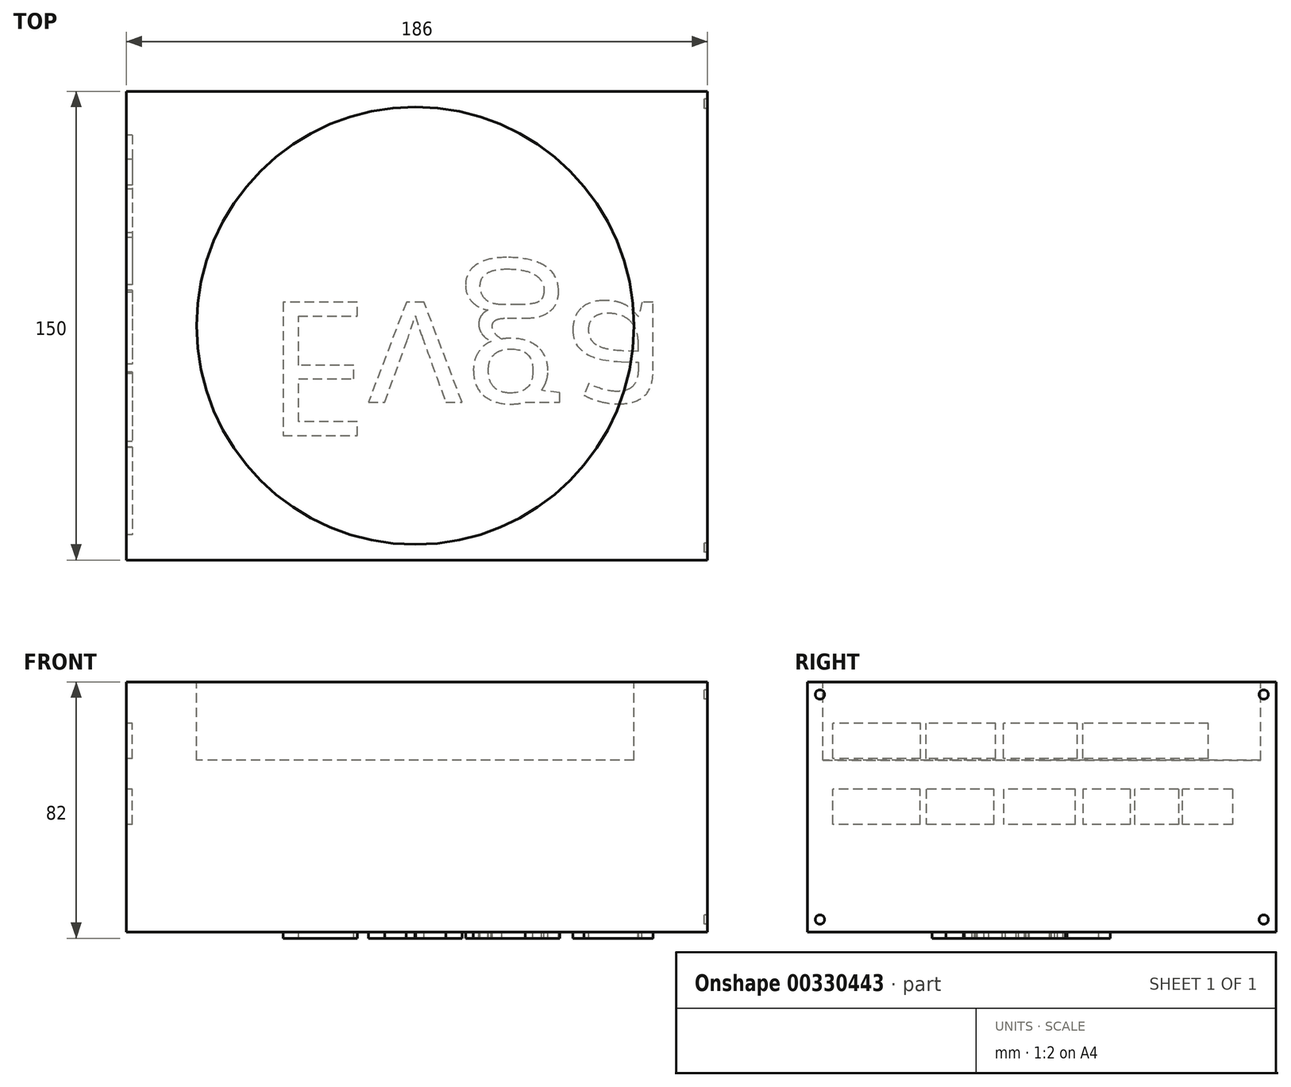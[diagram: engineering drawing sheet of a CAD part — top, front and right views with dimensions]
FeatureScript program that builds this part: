
annotation { "Feature Type Name" : "Feature", "Feature Type Description" : "" }
export const myFeature = defineFeature(function(context is Context, id is Id, definition is map)
    precondition{}
    {
        {
            var Q0;
            Q0=qCreatedBy(makeId("Top.planeOp"),FACE);
            var sketch = newSketch(context, id + "F0", { "sketchPlane" : qUnion([Q0])});
            skLineSegment(sketch, "E0.bottom", {"start": v(-3593.2, 0) * mm, "end": v(-3408.2, 0) * mm});
            skLineSegment(sketch, "E0.top", {"start": v(-3593.2, 150) * mm, "end": v(-3408.2, 150) * mm});
            skLineSegment(sketch, "E0.left", {"start": v(-3593.2, 0) * mm, "end": v(-3593.2, 150) * mm});
            skLineSegment(sketch, "E0.right", {"start": v(-3408.2, 0) * mm, "end": v(-3408.2, 150) * mm});
            skSolve(sketch);
        }
        {
            var Q0;
            Q0=makeQuery(id+"F0.imprint","IMPRINT",FACE,{"disambiguationData":[TD([[makeQuery(id+"F0.imprint","IMPRINT",EDGE,{"derivedFrom":sQuery(id+"F0.wireOp",EDGE,"E0.bottom")}),1.0]])]});
            extrude(context, id + "F1", {"entities" : qUnion([Q0]), "depth" : 80 * mm});
        }
        {
            var Q0;
            Q0=makeQuery(id+"F1.opExtrude","CAP_FACE",FACE,{"disambiguationData":[OSD([sQuery(id+"F0.wireOp",EDGE,"E0.bottom"),sQuery(id+"F0.wireOp",EDGE,"E0.top"),sQuery(id+"F0.wireOp",EDGE,"E0.left"),sQuery(id+"F0.wireOp",EDGE,"E0.right")])],"isStart":false});
            var sketch = newSketch(context, id + "F2", { "sketchPlane" : qUnion([Q0])});
            skLineSegment(sketch, "E1", {"start": v(-3593.2, 150) * mm, "end": v(-3408.2, 0) * mm, "construction": true});
            skCircle(sketch, "E2", {"center": v(-3500.7, 75) * mm, "radius": 70 * mm});
            skSolve(sketch);
        }
        {
            var Q0;
            Q0=makeQuery(id+"F2.imprint","IMPRINT",FACE,{"disambiguationData":[TD([[makeQuery(id+"F2.imprint","IMPRINT",EDGE,{"derivedFrom":sQuery(id+"F2.wireOp",EDGE,"E2")}),1.0]])]});
            extrude(context, id + "F3", {"entities" : qUnion([Q0]), "operationType" : NewBodyOperationType.REMOVE, "oppositeDirection" : true, "depth" : 25 * mm});
        }
        {
            var Q0;
            Q0=makeQuery(id+"F1.opExtrude","SWEPT_FACE",FACE,{"disambiguationData":[OSD([sQuery(id+"F0.wireOp",EDGE,"E0.right")])]});
            var sketch = newSketch(context, id + "F4", { "sketchPlane" : qUnion([Q0])});
            skLineSegment(sketch, "E3", {"start": v(0, 0) * mm, "end": v(0, 6) * mm});
            skLineSegment(sketch, "E4.bottom", {"start": v(114, 7.67) * mm, "end": v(126, 7.67) * mm});
            skLineSegment(sketch, "E4.top", {"start": v(114, 12.33) * mm, "end": v(126, 12.33) * mm});
            skLineSegment(sketch, "E4.right", {"start": v(126, 7.67) * mm, "end": v(126, 12.33) * mm});
            skLineSegment(sketch, "E5.bottom", {"start": v(116.68, 8.25) * mm, "end": v(123.32, 8.25) * mm});
            skLineSegment(sketch, "E5.top", {"start": v(116.68, 11.75) * mm, "end": v(123.32, 11.75) * mm});
            skLineSegment(sketch, "E5.right", {"start": v(123.32, 8.25) * mm, "end": v(123.32, 11.75) * mm});
            skLineSegment(sketch, "E6.bottom", {"start": v(114.02, 42.62) * mm, "end": v(125.98, 42.62) * mm});
            skLineSegment(sketch, "E6.top", {"start": v(114.02, 45.11) * mm, "end": v(125.98, 45.11) * mm});
            skLineSegment(sketch, "E6.right", {"start": v(125.98, 42.62) * mm, "end": v(125.98, 45.11) * mm});
            skCircle(sketch, "E7", {"center": v(128.98, 43.87) * mm, "radius": 1.5 * mm});
            skPoint(sketch, "E7.centerSnap0", {"position": v(125.98, 43.87) * mm});
            skLineSegment(sketch, "E8.MirrorCS", {"start": v(120, 21) * mm, "end": v(132, 21) * mm});
            skLineSegment(sketch, "E9.MirrorCS", {"start": v(132, 33) * mm, "end": v(130, 35) * mm});
            skLineSegment(sketch, "E10.MirrorCS", {"start": v(132, 35) * mm, "end": v(120, 35) * mm});
            skLineSegment(sketch, "E11.MirrorCS", {"start": v(132, 21) * mm, "end": v(132, 35) * mm});
            skPoint(sketch, "E12", {"position": v(4, 76) * mm});
            skLineSegment(sketch, "E13", {"start": v(75, 80) * mm, "end": v(75, 94.75) * mm, "construction": true});
            skLineSegment(sketch, "E14", {"start": v(0, 40) * mm, "end": v(-9.52, 40) * mm, "construction": true});
            skCircle(sketch, "E15", {"center": v(4, 76) * mm, "radius": 1.5 * mm});
            skPoint(sketch, "E16.MirrorP", {"position": v(146, 76) * mm});
            skCircle(sketch, "E17.MirrorC", {"center": v(146, 76) * mm, "radius": 1.5 * mm});
            skPoint(sketch, "E18.MirrorP", {"position": v(4, 4) * mm});
            skCircle(sketch, "E19.MirrorC", {"center": v(146, 4) * mm, "radius": 1.5 * mm});
            skCircle(sketch, "E20.MirrorC", {"center": v(4, 4) * mm, "radius": 1.5 * mm});
            skSolve(sketch);
        }
        {
            var Q0;
            Q0=makeQuery(id+"F1.opExtrude","CAP_FACE",FACE,{"disambiguationData":[OSD([sQuery(id+"F0.wireOp",EDGE,"E0.bottom"),sQuery(id+"F0.wireOp",EDGE,"E0.top"),sQuery(id+"F0.wireOp",EDGE,"E0.left"),sQuery(id+"F0.wireOp",EDGE,"E0.right")])],"isStart":true});
            var sketch = newSketch(context, id + "F5", { "sketchPlane" : qUnion([Q0])});
            skText(sketch, "E21", { "text": "Evga", "fontName": "OpenSans-Regular.ttf"});
            skPoint(sketch, "E21.firstSnap0", {"position": v(-3593.2, -75) * mm});
            const initialGuessF5  = {"E21": [-3.5489, -0.0825, 1, 0, 0.04302]};
            skSetInitialGuess(sketch, initialGuessF5);
            skSolve(sketch);
        }
        {
            var Q0;
            Q0=qSketchRegion(id+"F5",true);
            extrude(context, id + "F6", {"entities" : qUnion([Q0]), "operationType" : NewBodyOperationType.ADD, "depth" : 2 * mm});
        }
        {
            var Q0;
            {var subQ5=sQuery(id+"F4.wireOp",EDGE,"E5.left");Q0=makeQuery(id+"F4.imprint","IMPRINT",FACE,{"disambiguationData":[TD([[makeQuery(id+"F4.imprint","IMPRINT",EDGE,{"derivedFrom":subQ5}),-1.0]])]});}
            var Q1;
            {var subQ5=sQuery(id+"F4.wireOp",EDGE,"E5.right");Q1=makeQuery(id+"F4.imprint","IMPRINT",FACE,{"disambiguationData":[TD([[makeQuery(id+"F4.imprint","IMPRINT",EDGE,{"derivedFrom":subQ5}),1.0]])]});}
            var Q2;
            {var subQ0=sQuery(id+"F4.wireOp",EDGE,"E6.left");Q2=makeQuery(id+"F4.imprint","IMPRINT",FACE,{"disambiguationData":[TD([[makeQuery(id+"F4.imprint","IMPRINT",EDGE,{"derivedFrom":subQ0}),-1.0]])]});}
            var Q3;
            Q3=makeQuery(id+"F4.imprint","IMPRINT",FACE,{"disambiguationData":[TD([[makeQuery(id+"F4.imprint","IMPRINT",EDGE,{"derivedFrom":sQuery(id+"F4.wireOp",EDGE,"Howzav6s-LwVC-POIL-vaY7-dEpTv1sVQP2O")}),1.0]])]});
            var Q4;
            Q4=makeQuery(id+"F4.imprint","IMPRINT",FACE,{"disambiguationData":[TD([[makeQuery(id+"F4.imprint","IMPRINT",EDGE,{"derivedFrom":sQuery(id+"F4.wireOp",EDGE,"E7")}),1.0]])]});
            var Q5;
            Q5=makeQuery(id+"F4.imprint","IMPRINT",FACE,{"disambiguationData":[TD([[makeQuery(id+"F4.imprint","IMPRINT",EDGE,{"derivedFrom":sQuery(id+"F4.wireOp",EDGE,"60e5e2b8-d5ae-4825-a8f8-8ff2ab8d999b.10.8.0")}),-1.0]])]});
            var Q6;
            {var subQ15=sQuery(id+"F4.wireOp",EDGE,"E3");Q6=makeQuery(id+"F4.imprint","IMPRINT",FACE,{"disambiguationData":[TD([[makeQuery(id+"F4.imprint","IMPRINT",EDGE,{"derivedFrom":subQ15}),1.0]])]});}
            var Q7;
            {var subQ3=sQuery(id+"F4.wireOp",EDGE,"mJ3lwuVH-Yu2p-DGnq-pUDd-3jlMc4tZ1DTt");Q7=makeQuery(id+"F4.imprint","IMPRINT",FACE,{"disambiguationData":[TD([[makeQuery(id+"F4.imprint","IMPRINT",EDGE,{"derivedFrom":subQ3}),1.0]])]});}
            var Q8;
            {var subQ0=sQuery(id+"F4.wireOp",EDGE,"E9.MirrorCS");Q8=makeQuery(id+"F4.imprint","IMPRINT",FACE,{"disambiguationData":[TD([[makeQuery(id+"F4.imprint","IMPRINT",EDGE,{"derivedFrom":subQ0}),-1.0]])]});}
            extrude(context, id + "F7", {"entities" : qUnion([Q0, Q1, Q2, Q3, Q4, Q5, Q6, Q7, Q8]), "operationType" : NewBodyOperationType.ADD, "depth" : 1 * mm});
        }
        {
            var Q0;
            Q0=makeQuery(id+"F1.opExtrude","SWEPT_FACE",FACE,{"disambiguationData":[OSD([sQuery(id+"F0.wireOp",EDGE,"E0.left")])]});
            var sketch = newSketch(context, id + "F8", { "sketchPlane" : qUnion([Q0])});
            skSolve(sketch);
        }
        {
            var Q0;
            {var subQ0=sQuery(id+"F0.wireOp",EDGE,"E0.left");Q0=makeQuery(id+"F8.imprint","IMPRINT",FACE,{"disambiguationData":[TD([[makeQuery(id+"F8.imprint","IMPRINT",EDGE,{"derivedFrom":makeQuery(id+"F1.opExtrude","CAP_EDGE",EDGE,{"disambiguationData":[OSD([subQ0])],"isStart":true})}),-1.0]])]});}
            var sketch = newSketch(context, id + "F9", { "sketchPlane" : qUnion([Q0])});
            skLineSegment(sketch, "E22.bottom", {"start": v(-156.27, 55.54) * mm, "end": v(-8.06, 55.54) * mm});
            skLineSegment(sketch, "E22.top", {"start": v(-156.27, 66.8) * mm, "end": v(-8.06, 66.8) * mm});
            skLineSegment(sketch, "E22.left", {"start": v(-156.27, 55.54) * mm, "end": v(-156.27, 66.8) * mm});
            skLineSegment(sketch, "E22.right", {"start": v(-8.06, 55.54) * mm, "end": v(-8.06, 66.8) * mm});
            skLineSegment(sketch, "E23.bottom", {"start": v(-156.27, 34.4) * mm, "end": v(-8.06, 34.4) * mm});
            skLineSegment(sketch, "E23.top", {"start": v(-156.27, 45.65) * mm, "end": v(-8.06, 45.65) * mm});
            skLineSegment(sketch, "E23.left", {"start": v(-156.27, 34.4) * mm, "end": v(-156.27, 45.65) * mm});
            skLineSegment(sketch, "E23.right", {"start": v(-8.06, 34.4) * mm, "end": v(-8.06, 45.65) * mm});
            skLineSegment(sketch, "E24", {"start": v(-130.4, 55.54) * mm, "end": v(-130.4, 66.8) * mm});
            skLineSegment(sketch, "E25", {"start": v(-88.12, 55.54) * mm, "end": v(-88.12, 66.8) * mm});
            skLineSegment(sketch, "E26", {"start": v(-62.7, 55.54) * mm, "end": v(-62.7, 66.8) * mm});
            skLineSegment(sketch, "E27", {"start": v(-37.97, 55.54) * mm, "end": v(-37.97, 66.8) * mm});
            skLineSegment(sketch, "E28", {"start": v(-37.97, 45.65) * mm, "end": v(-37.97, 34.4) * mm});
            skLineSegment(sketch, "E29", {"start": v(-62.7, 45.65) * mm, "end": v(-62.7, 34.4) * mm});
            skLineSegment(sketch, "E30", {"start": v(-88.12, 45.65) * mm, "end": v(-88.12, 34.4) * mm});
            skLineSegment(sketch, "E31", {"start": v(-103.2, 45.65) * mm, "end": v(-103.2, 34.4) * mm});
            skLineSegment(sketch, "E32", {"start": v(-118.71, 45.65) * mm, "end": v(-118.71, 34.4) * mm});
            skLineSegment(sketch, "E33", {"start": v(-136.03, 45.65) * mm, "end": v(-136.03, 34.4) * mm});
            skLineSegment(sketch, "E34", {"start": v(-128.26, 55.54) * mm, "end": v(-128.26, 66.8) * mm});
            skLineSegment(sketch, "E35", {"start": v(-86.35, 55.54) * mm, "end": v(-86.35, 66.8) * mm});
            skLineSegment(sketch, "E36", {"start": v(-60.2, 55.54) * mm, "end": v(-60.2, 66.8) * mm});
            skLineSegment(sketch, "E37", {"start": v(-36.22, 55.54) * mm, "end": v(-36.22, 66.8) * mm});
            skLineSegment(sketch, "E38", {"start": v(-36.03, 34.4) * mm, "end": v(-36.03, 45.65) * mm});
            skLineSegment(sketch, "E39", {"start": v(-59.67, 34.4) * mm, "end": v(-59.67, 45.65) * mm});
            skLineSegment(sketch, "E40", {"start": v(-85.67, 34.4) * mm, "end": v(-85.67, 45.65) * mm});
            skLineSegment(sketch, "E41", {"start": v(-104.72, 34.4) * mm, "end": v(-104.72, 45.65) * mm});
            skLineSegment(sketch, "E42", {"start": v(-119.99, 34.4) * mm, "end": v(-119.99, 45.65) * mm});
            skLineSegment(sketch, "E43", {"start": v(-137.63, 34.4) * mm, "end": v(-137.63, 45.65) * mm});
            skSolve(sketch);
        }
        {
            var Q0;
            {var subQ0=sQuery(id+"F9.wireOp",EDGE,"E22.left");Q0=makeQuery(id+"F9.imprint","IMPRINT",FACE,{"disambiguationData":[TD([[makeQuery(id+"F9.imprint","IMPRINT",EDGE,{"derivedFrom":subQ0}),-1.0]])]});}
            var Q1;
            {var subQ0=sQuery(id+"F9.wireOp",EDGE,"E25");Q1=makeQuery(id+"F9.imprint","IMPRINT",FACE,{"disambiguationData":[TD([[makeQuery(id+"F9.imprint","IMPRINT",EDGE,{"derivedFrom":subQ0}),1.0]])]});}
            var Q2;
            {var subQ0=sQuery(id+"F9.wireOp",EDGE,"E26");Q2=makeQuery(id+"F9.imprint","IMPRINT",FACE,{"disambiguationData":[TD([[makeQuery(id+"F9.imprint","IMPRINT",EDGE,{"derivedFrom":subQ0}),1.0]])]});}
            var Q3;
            {var subQ0=sQuery(id+"F9.wireOp",EDGE,"E27");Q3=makeQuery(id+"F9.imprint","IMPRINT",FACE,{"disambiguationData":[TD([[makeQuery(id+"F9.imprint","IMPRINT",EDGE,{"derivedFrom":subQ0}),1.0]])]});}
            var Q4;
            {var subQ0=sQuery(id+"F9.wireOp",EDGE,"E22.right");Q4=makeQuery(id+"F9.imprint","IMPRINT",FACE,{"disambiguationData":[TD([[makeQuery(id+"F9.imprint","IMPRINT",EDGE,{"derivedFrom":subQ0}),1.0]])]});}
            var Q5;
            {var subQ0=sQuery(id+"F9.wireOp",EDGE,"E23.right");Q5=makeQuery(id+"F9.imprint","IMPRINT",FACE,{"disambiguationData":[TD([[makeQuery(id+"F9.imprint","IMPRINT",EDGE,{"derivedFrom":subQ0}),1.0]])]});}
            var Q6;
            {var subQ0=sQuery(id+"F9.wireOp",EDGE,"E29");Q6=makeQuery(id+"F9.imprint","IMPRINT",FACE,{"disambiguationData":[TD([[makeQuery(id+"F9.imprint","IMPRINT",EDGE,{"derivedFrom":subQ0}),-1.0]])]});}
            var Q7;
            {var subQ0=sQuery(id+"F9.wireOp",EDGE,"E33");Q7=makeQuery(id+"F9.imprint","IMPRINT",FACE,{"disambiguationData":[TD([[makeQuery(id+"F9.imprint","IMPRINT",EDGE,{"derivedFrom":subQ0}),1.0]])]});}
            var Q8;
            {var subQ0=sQuery(id+"F9.wireOp",EDGE,"E32");Q8=makeQuery(id+"F9.imprint","IMPRINT",FACE,{"disambiguationData":[TD([[makeQuery(id+"F9.imprint","IMPRINT",EDGE,{"derivedFrom":subQ0}),1.0]])]});}
            var Q9;
            {var subQ0=sQuery(id+"F9.wireOp",EDGE,"E30");Q9=makeQuery(id+"F9.imprint","IMPRINT",FACE,{"disambiguationData":[TD([[makeQuery(id+"F9.imprint","IMPRINT",EDGE,{"derivedFrom":subQ0}),-1.0]])]});}
            var Q10;
            {var subQ0=sQuery(id+"F9.wireOp",EDGE,"E23.left");Q10=makeQuery(id+"F9.imprint","IMPRINT",FACE,{"disambiguationData":[TD([[makeQuery(id+"F9.imprint","IMPRINT",EDGE,{"derivedFrom":subQ0}),-1.0]])]});}
            var Q11;
            {var subQ0=sQuery(id+"F9.wireOp",EDGE,"E28");Q11=makeQuery(id+"F9.imprint","IMPRINT",FACE,{"disambiguationData":[TD([[makeQuery(id+"F9.imprint","IMPRINT",EDGE,{"derivedFrom":subQ0}),-1.0]])]});}
            extrude(context, id + "F10", {"entities" : qUnion([Q0, Q1, Q2, Q3, Q4, Q5, Q6, Q7, Q8, Q9, Q10, Q11]), "operationType" : NewBodyOperationType.REMOVE, "oppositeDirection" : true, "depth" : 2 * mm});
        }
    });
